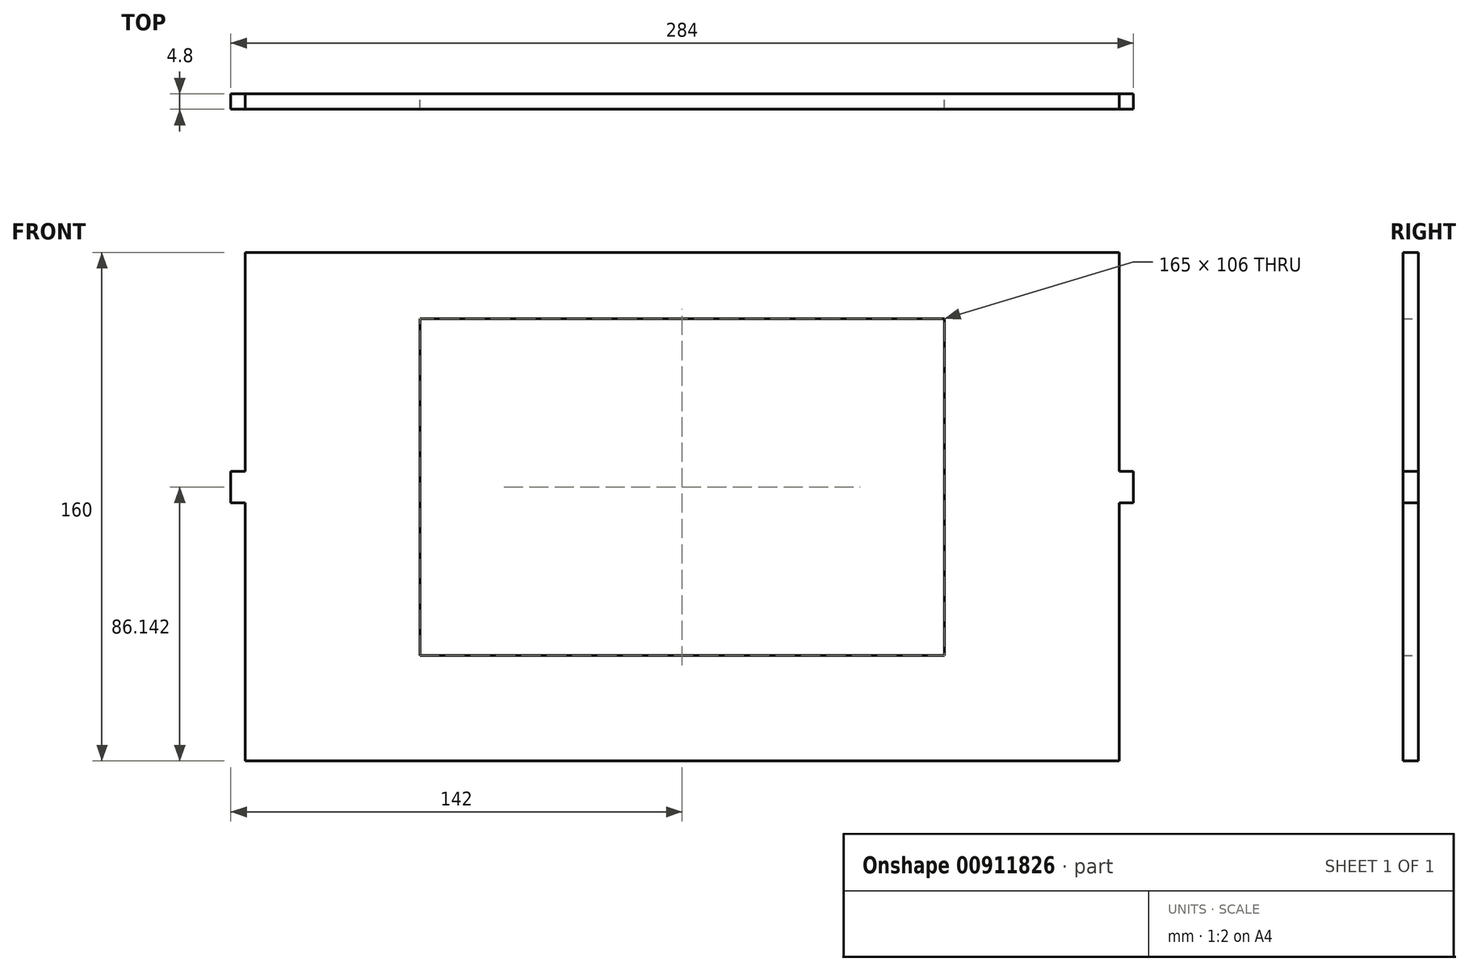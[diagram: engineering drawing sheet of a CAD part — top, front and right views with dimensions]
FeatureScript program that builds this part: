
annotation { "Feature Type Name" : "Feature", "Feature Type Description" : "" }
export const myFeature = defineFeature(function(context is Context, id is Id, definition is map)
    precondition{}
    {
        {
            var Q0;
            Q0=qCreatedBy(makeId("Front.planeOp"),FACE);
            var sketch = newSketch(context, id + "F0", { "sketchPlane" : qUnion([Q0])});
            skLineSegment(sketch, "E0.bottom", {"start": v(-174.16, 103.46) * mm, "end": v(100.84, 103.46) * mm});
            skLineSegment(sketch, "E0.top", {"start": v(-174.16, -56.54) * mm, "end": v(100.84, -56.54) * mm});
            skLineSegment(sketch, "E0.left", {"start": v(-174.16, 103.46) * mm, "end": v(-174.16, -56.54) * mm});
            skLineSegment(sketch, "E0.right", {"start": v(100.84, 103.46) * mm, "end": v(100.84, -56.54) * mm});
            skLineSegment(sketch, "E1.MirrorCS", {"start": v(100.84, 29.6) * mm, "end": v(105.34, 29.6) * mm});
            skLineSegment(sketch, "E2.MirrorCS", {"start": v(101.94, 29.6) * mm, "end": v(105.34, 29.6) * mm});
            skLineSegment(sketch, "E3.MirrorCS", {"start": v(105.34, 24.6) * mm, "end": v(101.94, 24.6) * mm});
            skLineSegment(sketch, "E4.MirrorCS", {"start": v(105.64, 34.6) * mm, "end": v(100.84, 34.6) * mm});
            skLineSegment(sketch, "E5.bottom", {"start": v(-119.16, 82.6) * mm, "end": v(45.84, 82.6) * mm});
            skLineSegment(sketch, "E5.top", {"start": v(-119.16, -23.4) * mm, "end": v(45.84, -23.4) * mm});
            skLineSegment(sketch, "E5.left", {"start": v(-119.16, 82.6) * mm, "end": v(-119.16, -23.4) * mm});
            skLineSegment(sketch, "E5.right", {"start": v(45.84, 82.6) * mm, "end": v(45.84, -23.4) * mm});
            skPoint(sketch, "E5.middle", {"position": v(-36.66, 29.6) * mm});
            skPoint(sketch, "E5.middle.positionSnap0", {"position": v(-36.66, 103.46) * mm});
            skPoint(sketch, "E5.centerSnap0", {"position": v(-36.66, 103.46) * mm});
            skLineSegment(sketch, "E6", {"start": v(105.34, 29.6) * mm, "end": v(105.34, 34.6) * mm});
            skLineSegment(sketch, "E7", {"start": v(105.34, 34.6) * mm, "end": v(105.34, 24.6) * mm});
            skLineSegment(sketch, "E8", {"start": v(105.34, 24.6) * mm, "end": v(100.84, 24.6) * mm});
            skLineSegment(sketch, "E9", {"start": v(-36.66, 103.46) * mm, "end": v(-36.66, -56.54) * mm});
            skLineSegment(sketch, "E10.MirrorCS", {"start": v(-178.66, 29.6) * mm, "end": v(-178.66, 34.6) * mm});
            skLineSegment(sketch, "E11.MirrorCS", {"start": v(-178.66, 34.6) * mm, "end": v(-178.66, 24.6) * mm});
            skLineSegment(sketch, "E12.MirrorCS", {"start": v(-174.16, 29.6) * mm, "end": v(-178.66, 29.6) * mm});
            skLineSegment(sketch, "E13.MirrorCS", {"start": v(-175.26, 29.6) * mm, "end": v(-178.66, 29.6) * mm});
            skLineSegment(sketch, "E14.MirrorCS", {"start": v(-178.66, 24.6) * mm, "end": v(-174.16, 24.6) * mm});
            skLineSegment(sketch, "E15.MirrorCS", {"start": v(-178.96, 34.6) * mm, "end": v(-174.16, 34.6) * mm});
            skLineSegment(sketch, "E16.MirrorCS", {"start": v(-178.66, 24.6) * mm, "end": v(-175.26, 24.6) * mm});
            skPoint(sketch, "E17.orphan", {"position": v(106.74, 24.6) * mm});
            skPoint(sketch, "E18.orphan", {"position": v(-180.06, 24.6) * mm});
            skPoint(sketch, "E19.MirrorCS.end.orphan", {"position": v(-175.26, 24.6) * mm});
            skSolve(sketch);
        }
        {
            var Q0;
            {var subQ3=sQuery(id+"F0.wireOp",EDGE,"E0.bottom");Q0=makeQuery(id+"F0.imprint","IMPRINT",FACE,{"disambiguationData":[TD([[makeQuery(id+"F0.imprint","IMPRINT",EDGE,{"derivedFrom":subQ3}),-1.0]])]});}
            var Q1;
            {var subQ0=sQuery(id+"F0.wireOp",EDGE,"e48a3bb5-675e-42eb-a290-356319898c6b3.MirrorCS");Q1=makeQuery(id+"F0.imprint","IMPRINT",FACE,{"disambiguationData":[TD([[makeQuery(id+"F0.imprint","IMPRINT",EDGE,{"derivedFrom":subQ0}),-1.0]])]});}
            var Q2;
            Q2=makeQuery(id+"F0.imprint","IMPRINT",FACE,{"disambiguationData":[TD([[makeQuery(id+"F0.imprint","IMPRINT",EDGE,{"derivedFrom":sQuery(id+"F0.wireOp",EDGE,"e48a3bb5-675e-42eb-a290-356319898c6b1.MirrorCS")}),1.0]])]});
            var Q3;
            {var subQ0=sQuery(id+"F0.wireOp",EDGE,"E2.MirrorCS");Q3=makeQuery(id+"F0.imprint","IMPRINT",FACE,{"disambiguationData":[TD([[makeQuery(id+"F0.imprint","IMPRINT",EDGE,{"derivedFrom":subQ0}),1.0]])]});}
            var Q4;
            {var subQ0=sQuery(id+"F0.wireOp",EDGE,"E2.MirrorCS");Q4=makeQuery(id+"F0.imprint","IMPRINT",FACE,{"disambiguationData":[TD([[makeQuery(id+"F0.imprint","IMPRINT",EDGE,{"derivedFrom":subQ0}),-1.0]])]});}
            var Q5;
            {var subQ5=sQuery(id+"F0.wireOp",EDGE,"e48a3bb5-675e-42eb-a290-356319898c6b5.MirrorCS");var subQ7=makeQuery(id+"F0.imprint","IMPRINT",VERTEX,{"derivedFrom":subQ5});Q5=makeQuery(id+"F0.imprint","IMPRINT",FACE,{"disambiguationData":[TD([[makeQuery(id+"F0.imprint","IMPRINT",EDGE,{"disambiguationData":[TD([[subQ7,1.0]])],"derivedFrom":subQ5}),-1.0]])]});}
            var Q6;
            {var subQ6=sQuery(id+"F0.wireOp",EDGE,"W8B56JJR-NiTp-jr3x-Jou0-mrKQW3mr2Dtd");Q6=makeQuery(id+"F0.imprint","IMPRINT",FACE,{"disambiguationData":[TD([[makeQuery(id+"F0.imprint","IMPRINT",EDGE,{"derivedFrom":subQ6}),1.0]])]});}
            var Q7;
            {var subQ0=sQuery(id+"F0.wireOp",EDGE,"E1.MirrorCS");var subQ3=makeQuery(id+"F0.imprint","IMPRINT",VERTEX,{"derivedFrom":subQ0});Q7=makeQuery(id+"F0.imprint","IMPRINT",FACE,{"disambiguationData":[TD([[makeQuery(id+"F0.imprint","IMPRINT",EDGE,{"disambiguationData":[TD([[subQ3,1.0]])],"derivedFrom":subQ0}),1.0]])]});}
            var Q8;
            {var subQ3=sQuery(id+"F0.wireOp",EDGE,"E1.MirrorCS");var subQ5=makeQuery(id+"F0.imprint","IMPRINT",VERTEX,{"derivedFrom":subQ3});Q8=makeQuery(id+"F0.imprint","IMPRINT",FACE,{"disambiguationData":[TD([[makeQuery(id+"F0.imprint","IMPRINT",EDGE,{"disambiguationData":[TD([[subQ5,1.0]])],"derivedFrom":subQ3}),-1.0]])]});}
            var Q9;
            {var subQ6=sQuery(id+"F0.wireOp",EDGE,"E10.MirrorCS");Q9=makeQuery(id+"F0.imprint","IMPRINT",FACE,{"disambiguationData":[TD([[makeQuery(id+"F0.imprint","IMPRINT",EDGE,{"derivedFrom":subQ6}),-1.0]])]});}
            var Q10;
            {var subQ1=sQuery(id+"F0.wireOp",EDGE,"E14.MirrorCS");Q10=makeQuery(id+"F0.imprint","IMPRINT",FACE,{"disambiguationData":[TD([[makeQuery(id+"F0.imprint","IMPRINT",EDGE,{"derivedFrom":subQ1}),1.0]])]});}
            extrude(context, id + "F1", {"entities" : qUnion([Q0, Q1, Q2, Q3, Q4, Q5, Q6, Q7, Q8, Q9, Q10]), "depth" : 4.8 * mm, "offsetDistance" : 25 * mm});
        }
    });
